# Revit family: Hager-GOLF-Surface_mounted-IP40-With_Cover-With_DIN-Hosted-FR-fr
name_source: partatom
category: Electrical Equipment
units: mm (PartAtom-declared; Revit-internal decimal feet)

## family parameters
Cut with Voids When Loaded = No
Host = Face
Maintain Annotation Orientation = Yes
Panel Configuration = Two Columns, Circuits Across
Part Type = Panelboard
Room Calculation Point = No
Round Connector Dimension = Use Diameter
Shared = No

## types (13) — shared parameters
BC_MODEL_ID = 1554323
BC_OBJECT_ID = 513872
BC_OBJECT_VERSION = #3
Code hager = ADD-EC000214_EU
EF000003 - mode de pose = saillie
EF000007 - couleur = blanc
EF000024 - résistant aux UV = No
EF000049 - profondeur = 99 mm  [stored 0.324803 ft]
EF000116 - numéro RAL = 9010
EF000118 - avec cadre/support de montage = No
EF001062 - finition CEM = No
EF001088 - possibilité de montage en saillie = Yes
EF001134 - rail DIN = Yes
EF004462 - type de fermeture = autre
EF005474 - indice de protection (IP) = IP40
EF006306 - avec serrure = No
EF009212 - finition du couvercle = fermé
EF015776 - borne de mise à la terre = Yes
EF015941 - porte pour transmission du signal = Yes
ETIM class code = EC000214
ETIM class name = Small distribution board
HG000001-nombre de colonnes = 1
HG000002-avec porte = Yes
HG000003-Gamme = GOLF
HG000005-Epaisseur = 2 mm  [stored 0.00656168 ft]
HG000006-Encastré = No
HG000009-Porte à double battant = No
HG000010-Portes asymétriques = No
HG000011-Rangées du bas vides = No
HG000012-Angle de pivotement de la porte = 90.00°
HG000013-Porte à gauche = No
HG000014-Porte à droite = Yes
HG000015-Visibilité de l'emprise de la porte = Yes
HG000016-Visibilité de la porte 3D = Yes
HG000017-Distance entre pôles = 18 mm  [stored 0.0590551 ft]
HG000060-RAL-number = 9010
HG000099-ID modèle Onfly = 507532
Manufacturer = Hager
Name = GOLF-Surface_mounted-IP40-With_Cover-With_DIN-FR
Name BIM&CO = Electricity
Name hager = ADD_Enclosures_EC000214
Uniformat = Low Tension Service & Dist.
Uniformat code = D501001
zero-valued in all types: Default Elevation, EF000218 - profondeur d'encastrement, EF000332 - hauteur d'encastrement, EF000846 - largeur d'encastrement, EF001131 - profondeur intérieure, HG000007-Nombre de colonnes vides, HG000008-Nombre de rangées vides

## per-type parameters (varying)
| type | BC_VARIANT_ID | EF000008 - largeur | EF000040 - hauteur | EF000266 - nombre de rangées | EF002950 - largeur en nombre de modules | EF006244 - couvercle/porte transparent(e) | EF015777 - borne à conducteur neutre | HG000004-Référence fabricant | HGEF000266-Nombre de rangées | HGEF0002950-largeur en nombre de modules |
| GOLF-Surface_mounted_W138_H184_D99_4_Modular_Spacing-VS104PR | 1178877 | 138 mm  [stored 0.452756 ft] | 184 mm  [stored 0.603675 ft] | 1 | 4 | No | No | VS104PR | 1 | 4 |
| GOLF-Surface_mounted_W138_H184_D99_4_Modular_Spacing-VS104TR | 1178878 | 138 mm  [stored 0.452756 ft] | 184 mm  [stored 0.603675 ft] | 1 | 4 | Yes | No | VS104TR | 1 | 4 |
| GOLF-Surface_mounted_W210_H184_D99_8_Modular_Spacing-VS108PR | 1178879 | 210 mm  [stored 0.688976 ft] | 184 mm  [stored 0.603675 ft] | 1 | 8 | No | No | VS108PR | 1 | 8 |
| GOLF-Surface_mounted_W210_H184_D99_8_Modular_Spacing-VS108TR | 1178880 | 210 mm  [stored 0.688976 ft] | 184 mm  [stored 0.603675 ft] | 1 | 8 | Yes | No | VS108TR | 1 | 8 |
| GOLF-Surface_mounted_W282_H252_D99_12_Modular_Spacing-VS112PR | 1178881 | 282 mm | 252 mm  [stored 0.826772 ft] | 1 | 12 | No | No | VS112PR | 1 | 12 |
| GOLF-Surface_mounted_W282_H252_D99_12_Modular_Spacing-VS112TR | 1178882 | 282 mm | 252 mm  [stored 0.826772 ft] | 1 | 12 | Yes | No | VS112TR | 1 | 12 |
| GOLF-Surface_mounted_W282_H377_D99_12_Modular_Spacing-VS212PR | 1178883 | 282 mm | 377 mm  [stored 1.23688 ft] | 2 | 12 | No | Yes | VS212PR | 2 | 12 |
| GOLF-Surface_mounted_W282_H377_D99_12_Modular_Spacing-VS212TR | 1178885 | 282 mm | 377 mm  [stored 1.23688 ft] | 2 | 12 | Yes | Yes | VS212TR | 2 | 12 |
| GOLF-Surface_mounted_W282_H500_D99_12_Modular_Spacing-VS312PR | 1178887 | 282 mm | 500 mm  [stored 1.64042 ft] | 3 | 12 | No | Yes | VS312PR | 3 | 12 |
| GOLF-Surface_mounted_W282_H500_D99_12_Modular_Spacing-VS312TR | 1178889 | 282 mm | 500 mm  [stored 1.64042 ft] | 3 | 12 | Yes | Yes | VS312TR | 3 | 12 |
| GOLF-Surface_mounted_W282_H647_D99_12_Modular_Spacing-VS412PR | 1178891 | 282 mm | 647 mm  [stored 2.1227 ft] | 4 | 12 | No | Yes | VS412PR | 4 | 12 |
| GOLF-Surface_mounted_W282_H647_D99_12_Modular_Spacing-VS412TR | 1178893 | 282 mm | 647 mm  [stored 2.1227 ft] | 4 | 12 | Yes | Yes | VS412TR | 4 | 12 |
| GOLF-Surface_mounted_W390_H647_D99_18_Modular_Spacing-VS418PR | 1178895 | 390 mm  [stored 1.27953 ft] | 647 mm  [stored 2.1227 ft] | 4 | 18 | No | Yes | VS418PR | 4 | 18 |

note: column(s) folded — value = type name in every type: Reference

note: [stored X ft] marks values corroborated as IEEE doubles in the binary element streams (Revit-internal decimal feet)

## geometry (parser evidence)
native form markers: Sweep x14
no freeform markers — native parametric forms only
